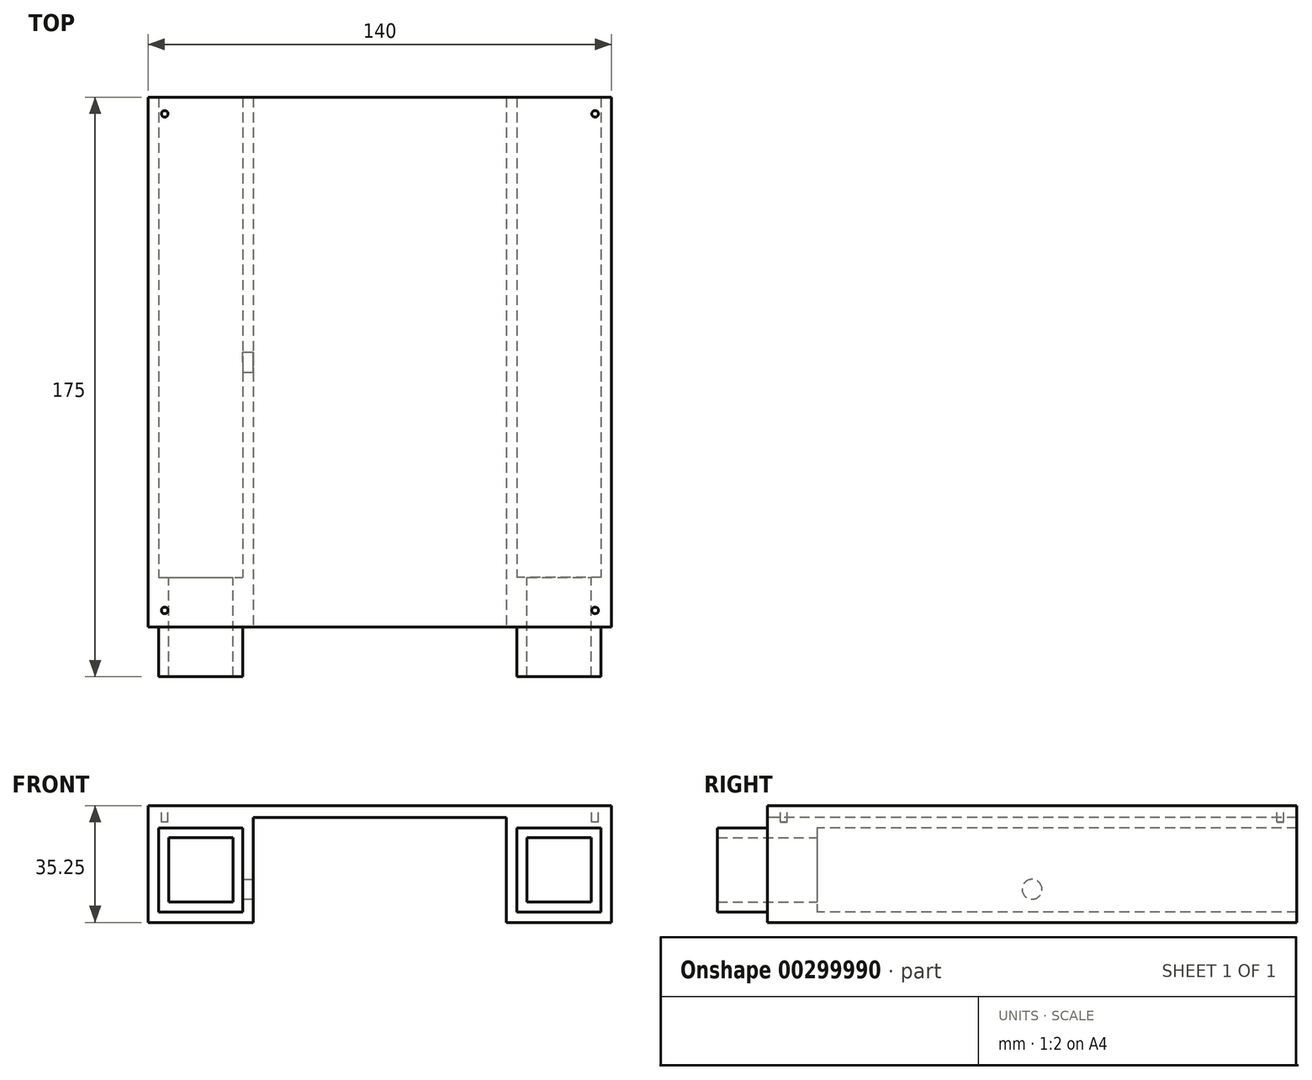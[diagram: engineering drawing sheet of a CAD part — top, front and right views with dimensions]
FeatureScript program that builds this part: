
annotation { "Feature Type Name" : "Feature", "Feature Type Description" : "" }
export const myFeature = defineFeature(function(context is Context, id is Id, definition is map)
    precondition{}
    {
        {
            var Q0;
            Q0=qCreatedBy(makeId("Top.planeOp"),FACE);
            var sketch = newSketch(context, id + "F0", { "sketchPlane" : qUnion([Q0])});
            skLineSegment(sketch, "E0.bottom", {"start": v(-71.28, 117.03) * mm, "end": v(68.72, 117.03) * mm});
            skLineSegment(sketch, "E0.top", {"start": v(-71.28, -42.97) * mm, "end": v(68.72, -42.97) * mm});
            skLineSegment(sketch, "E0.left", {"start": v(-71.28, 117.03) * mm, "end": v(-71.28, -42.97) * mm});
            skLineSegment(sketch, "E0.right", {"start": v(68.72, 117.03) * mm, "end": v(68.72, -42.97) * mm});
            skSolve(sketch);
        }
        {
            var Q0;
            Q0=makeQuery(id+"F0.imprint","IMPRINT",FACE,{"disambiguationData":[TD([[makeQuery(id+"F0.imprint","IMPRINT",EDGE,{"derivedFrom":sQuery(id+"F0.wireOp",EDGE,"E0.bottom")}),-1.0]])]});
            extrude(context, id + "F1", {"entities" : qUnion([Q0]), "depth" : 3.5 * mm});
        }
        {
            var Q0;
            Q0=makeQuery(id+"F1.opExtrude","SWEPT_FACE",FACE,{"disambiguationData":[OSD([sQuery(id+"F0.wireOp",EDGE,"E0.top")])]});
            var sketch = newSketch(context, id + "F2", { "sketchPlane" : qUnion([Q0])});
            skLineSegment(sketch, "E1.bottom", {"start": v(-71.28, 0) * mm, "end": v(-39.53, 0) * mm});
            skLineSegment(sketch, "E1.top", {"start": v(-71.28, -31.75) * mm, "end": v(-39.53, -31.75) * mm});
            skLineSegment(sketch, "E1.left", {"start": v(-71.28, 0) * mm, "end": v(-71.28, -31.75) * mm});
            skLineSegment(sketch, "E1.right", {"start": v(-39.53, 0) * mm, "end": v(-39.53, -31.75) * mm});
            skLineSegment(sketch, "E2.bottom", {"start": v(-68.1, -3.17) * mm, "end": v(-42.7, -3.17) * mm});
            skLineSegment(sketch, "E2.top", {"start": v(-68.1, -28.58) * mm, "end": v(-42.7, -28.58) * mm});
            skLineSegment(sketch, "E2.left", {"start": v(-68.1, -3.17) * mm, "end": v(-68.1, -28.57) * mm});
            skLineSegment(sketch, "E2.right", {"start": v(-42.7, -3.17) * mm, "end": v(-42.7, -28.58) * mm});
            skLineSegment(sketch, "E3.bottom", {"start": v(68.72, 0) * mm, "end": v(36.97, 0) * mm});
            skLineSegment(sketch, "E3.top", {"start": v(68.72, -31.75) * mm, "end": v(36.97, -31.75) * mm});
            skLineSegment(sketch, "E3.left", {"start": v(68.72, 0) * mm, "end": v(68.72, -31.75) * mm});
            skLineSegment(sketch, "E3.right", {"start": v(36.97, 0) * mm, "end": v(36.97, -31.75) * mm});
            skLineSegment(sketch, "E4.bottom", {"start": v(65.55, -3.17) * mm, "end": v(40.15, -3.18) * mm});
            skLineSegment(sketch, "E4.top", {"start": v(65.55, -28.57) * mm, "end": v(40.15, -28.57) * mm});
            skLineSegment(sketch, "E4.left", {"start": v(65.55, -3.17) * mm, "end": v(65.55, -28.57) * mm});
            skLineSegment(sketch, "E4.right", {"start": v(40.15, -3.18) * mm, "end": v(40.15, -28.57) * mm});
            skSolve(sketch);
        }
        {
            var Q0;
            Q0=qSketchRegion(id+"F2",true);
            extrude(context, id + "F3", {"entities" : qUnion([Q0]), "operationType" : NewBodyOperationType.ADD, "oppositeDirection" : true, "depth" : 160 * mm});
        }
        {
            var Q0;
            Q0=makeQuery(id+"F3.boolean.opBoolean","MERGE",FACE,{"derivedFrom":[makeQuery(id+"F1.opExtrude","SWEPT_FACE",FACE,{"disambiguationData":[OSD([sQuery(id+"F0.wireOp",EDGE,"E0.top")])]}),makeQuery(id+"F3.opExtrude","CAP_FACE",FACE,{"disambiguationData":[OSD([sQuery(id+"F2.wireOp",EDGE,"E1.bottom"),sQuery(id+"F2.wireOp",EDGE,"E1.top"),sQuery(id+"F2.wireOp",EDGE,"E1.left"),sQuery(id+"F2.wireOp",EDGE,"E1.right"),sQuery(id+"F2.wireOp",EDGE,"E2.bottom"),sQuery(id+"F2.wireOp",EDGE,"E2.top"),sQuery(id+"F2.wireOp",EDGE,"E2.left"),sQuery(id+"F2.wireOp",EDGE,"E2.right")])],"isStart":true}),makeQuery(id+"F3.opExtrude","CAP_FACE",FACE,{"disambiguationData":[OSD([sQuery(id+"F2.wireOp",EDGE,"E3.bottom"),sQuery(id+"F2.wireOp",EDGE,"E3.top"),sQuery(id+"F2.wireOp",EDGE,"E3.left"),sQuery(id+"F2.wireOp",EDGE,"E3.right"),sQuery(id+"F2.wireOp",EDGE,"E4.bottom"),sQuery(id+"F2.wireOp",EDGE,"E4.top"),sQuery(id+"F2.wireOp",EDGE,"E4.left"),sQuery(id+"F2.wireOp",EDGE,"E4.right")])],"isStart":true})]});
            var sketch = newSketch(context, id + "F4", { "sketchPlane" : qUnion([Q0])});
            skLineSegment(sketch, "E5.bottom", {"start": v(-68.1, -3.17) * mm, "end": v(-42.7, -3.17) * mm});
            skLineSegment(sketch, "E5.top", {"start": v(-68.1, -28.58) * mm, "end": v(-42.7, -28.58) * mm});
            skLineSegment(sketch, "E5.left", {"start": v(-68.1, -3.17) * mm, "end": v(-68.1, -28.58) * mm});
            skLineSegment(sketch, "E5.right", {"start": v(-42.7, -3.18) * mm, "end": v(-42.7, -28.58) * mm});
            skLineSegment(sketch, "E6.bottom", {"start": v(40.15, -3.18) * mm, "end": v(65.55, -3.18) * mm});
            skLineSegment(sketch, "E6.top", {"start": v(40.15, -28.57) * mm, "end": v(65.55, -28.57) * mm});
            skLineSegment(sketch, "E6.left", {"start": v(40.15, -3.18) * mm, "end": v(40.15, -28.57) * mm});
            skLineSegment(sketch, "E6.right", {"start": v(65.55, -3.18) * mm, "end": v(65.55, -28.57) * mm});
            skLineSegment(sketch, "E7.bottom", {"start": v(-65.1, -6.17) * mm, "end": v(-45.7, -6.17) * mm});
            skLineSegment(sketch, "E7.top", {"start": v(-65.1, -25.58) * mm, "end": v(-45.7, -25.58) * mm});
            skLineSegment(sketch, "E7.left", {"start": v(-65.1, -6.17) * mm, "end": v(-65.1, -25.58) * mm});
            skLineSegment(sketch, "E7.right", {"start": v(-45.7, -6.17) * mm, "end": v(-45.7, -25.58) * mm});
            skLineSegment(sketch, "E8.bottom", {"start": v(43.15, -6.18) * mm, "end": v(62.55, -6.18) * mm});
            skLineSegment(sketch, "E8.top", {"start": v(43.15, -25.57) * mm, "end": v(62.55, -25.57) * mm});
            skLineSegment(sketch, "E8.left", {"start": v(43.15, -6.18) * mm, "end": v(43.15, -25.57) * mm});
            skLineSegment(sketch, "E8.right", {"start": v(62.55, -6.18) * mm, "end": v(62.55, -25.57) * mm});
            skSolve(sketch);
        }
        {
            var Q0;
            Q0=qSketchRegion(id+"F4",true);
            extrude(context, id + "F5", {"entities" : qUnion([Q0]), "operationType" : NewBodyOperationType.ADD, "endBound" : BoundingType.SYMMETRIC, "depth" : 30 * mm});
        }
        {
            var Q0;
            Q0=makeQuery(id+"F3.opExtrude","SWEPT_FACE",FACE,{"disambiguationData":[OSD([sQuery(id+"F2.wireOp",EDGE,"E1.right")])]});
            var sketch = newSketch(context, id + "F6", { "sketchPlane" : qUnion([Q0])});
            skCircle(sketch, "E9", {"center": v(37.03, -21.75) * mm, "radius": 3 * mm});
            skSolve(sketch);
        }
        {
            var Q0;
            Q0 = qSketchRegion(id + "F6", true);
            extrude(context, id + "F7", {"entities" : qUnion([Q0]), "operationType" : NewBodyOperationType.REMOVE, "oppositeDirection" : true, "depth" : 4 * mm});
        }
        {
            var Q0;
            Q0=makeQuery(id+"F1.opExtrude","CAP_FACE",FACE,{"disambiguationData":[OSD([sQuery(id+"F0.wireOp",EDGE,"E0.bottom"),sQuery(id+"F0.wireOp",EDGE,"E0.top"),sQuery(id+"F0.wireOp",EDGE,"E0.left"),sQuery(id+"F0.wireOp",EDGE,"E0.right")])],"isStart":false});
            var sketch = newSketch(context, id + "F8", { "sketchPlane" : qUnion([Q0])});
            skCircle(sketch, "E10", {"center": v(-66.28, 112.03) * mm, "radius": 1 * mm});
            skCircle(sketch, "E11", {"center": v(63.72, 112.03) * mm, "radius": 1 * mm});
            skCircle(sketch, "E12", {"center": v(63.72, -37.97) * mm, "radius": 1 * mm});
            skCircle(sketch, "E13", {"center": v(-66.28, -37.97) * mm, "radius": 1 * mm});
            skSolve(sketch);
        }
        {
            var Q0;
            Q0 = qSketchRegion(id + "F8", true);
            extrude(context, id + "F9", {"entities" : qUnion([Q0]), "operationType" : NewBodyOperationType.REMOVE, "oppositeDirection" : true, "depth" : 5 * mm});
        }
    });
